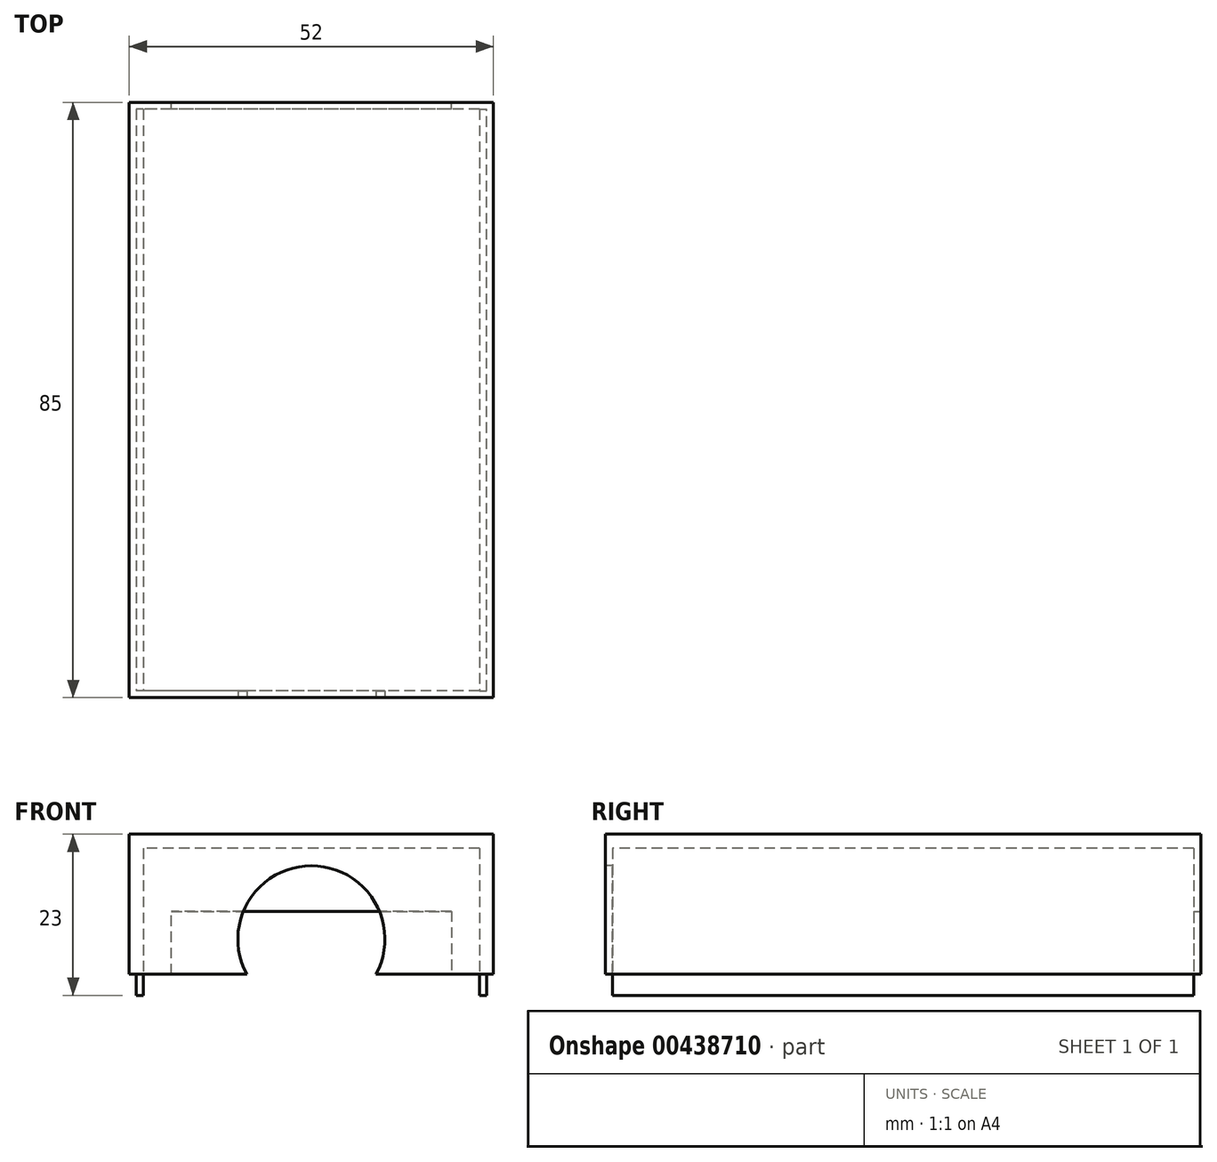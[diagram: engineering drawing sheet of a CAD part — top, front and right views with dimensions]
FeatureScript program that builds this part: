
annotation { "Feature Type Name" : "Feature", "Feature Type Description" : "" }
export const myFeature = defineFeature(function(context is Context, id is Id, definition is map)
    precondition{}
    {
        {
            var Q0;
            Q0=qCreatedBy(makeId("Top.planeOp"),FACE);
            var sketch = newSketch(context, id + "F0", { "sketchPlane" : qUnion([Q0])});
            skLineSegment(sketch, "E0.bottom", {"start": v(26, -42.5) * mm, "end": v(-26, -42.5) * mm});
            skLineSegment(sketch, "E0.top", {"start": v(26, 42.5) * mm, "end": v(-26, 42.5) * mm});
            skLineSegment(sketch, "E0.left", {"start": v(26, -42.5) * mm, "end": v(26, 42.5) * mm});
            skLineSegment(sketch, "E0.right", {"start": v(-26, -42.5) * mm, "end": v(-26, 42.5) * mm});
            skPoint(sketch, "E0.middle", {"position": v(0, 0) * mm});
            skSolve(sketch);
        }
        {
            var Q0;
            Q0 = qSketchRegion(id + "F0", true);
            extrude(context, id + "F1", {"entities" : qUnion([Q0]), "depth" : 20 * mm});
        }
        {
            var Q0;
            Q0=makeQuery(id+"F1.opExtrude","CAP_FACE",FACE,{"disambiguationData":[OSD([sQuery(id+"F0.wireOp",EDGE,"E0.bottom"),sQuery(id+"F0.wireOp",EDGE,"E0.top"),sQuery(id+"F0.wireOp",EDGE,"E0.left"),sQuery(id+"F0.wireOp",EDGE,"E0.right")])],"isStart":true});
            var sketch = newSketch(context, id + "F2", { "sketchPlane" : qUnion([Q0])});
            skLineSegment(sketch, "E1.bottom", {"start": v(24, -41.5) * mm, "end": v(-24, -41.5) * mm});
            skLineSegment(sketch, "E1.top", {"start": v(24, 41.5) * mm, "end": v(-24, 41.5) * mm});
            skLineSegment(sketch, "E1.left", {"start": v(24, -41.5) * mm, "end": v(24, 41.5) * mm});
            skLineSegment(sketch, "E1.right", {"start": v(-24, -41.5) * mm, "end": v(-24, 41.5) * mm});
            skPoint(sketch, "E1.middle", {"position": v(0, 0) * mm});
            skSolve(sketch);
        }
        {
            var Q0;
            Q0=makeQuery(id+"F2.imprint","IMPRINT",FACE,{"disambiguationData":[TD([[makeQuery(id+"F2.imprint","IMPRINT",EDGE,{"derivedFrom":sQuery(id+"F2.wireOp",EDGE,"E1.bottom")}),-1.0]])]});
            extrude(context, id + "F3", {"entities" : qUnion([Q0]), "operationType" : NewBodyOperationType.REMOVE, "oppositeDirection" : true, "depth" : 18 * mm});
        }
        {
            var Q0;
            Q0=makeQuery(id+"F1.opExtrude","CAP_FACE",FACE,{"disambiguationData":[OSD([sQuery(id+"F0.wireOp",EDGE,"E0.bottom"),sQuery(id+"F0.wireOp",EDGE,"E0.top"),sQuery(id+"F0.wireOp",EDGE,"E0.left"),sQuery(id+"F0.wireOp",EDGE,"E0.right")])],"isStart":true});
            var sketch = newSketch(context, id + "F4", { "sketchPlane" : qUnion([Q0])});
            skLineSegment(sketch, "E2.bottom", {"start": v(-24, -41.5) * mm, "end": v(-25, -41.5) * mm});
            skLineSegment(sketch, "E2.top", {"start": v(-24, 41.5) * mm, "end": v(-25, 41.5) * mm});
            skLineSegment(sketch, "E2.left", {"start": v(-24, -41.5) * mm, "end": v(-24, 41.5) * mm});
            skLineSegment(sketch, "E2.right", {"start": v(-25, -41.5) * mm, "end": v(-25, 41.5) * mm});
            skLineSegment(sketch, "E3.bottom", {"start": v(24, 41.5) * mm, "end": v(25, 41.5) * mm});
            skLineSegment(sketch, "E3.top", {"start": v(24, -41.5) * mm, "end": v(25, -41.5) * mm});
            skLineSegment(sketch, "E3.left", {"start": v(24, 41.5) * mm, "end": v(24, -41.5) * mm});
            skLineSegment(sketch, "E3.right", {"start": v(25, 41.5) * mm, "end": v(25, -41.5) * mm});
            skSolve(sketch);
        }
        {
            var Q0;
            Q0=makeQuery(id+"F4.imprint","IMPRINT",FACE,{"disambiguationData":[TD([[makeQuery(id+"F4.imprint","IMPRINT",EDGE,{"derivedFrom":sQuery(id+"F4.wireOp",EDGE,"E2.bottom")}),-1.0]])]});
            var Q1;
            Q1=makeQuery(id+"F4.imprint","IMPRINT",FACE,{"disambiguationData":[TD([[makeQuery(id+"F4.imprint","IMPRINT",EDGE,{"derivedFrom":sQuery(id+"F4.wireOp",EDGE,"E3.bottom")}),-1.0]])]});
            extrude(context, id + "F5", {"entities" : qUnion([Q0, Q1]), "operationType" : NewBodyOperationType.ADD, "depth" : 3 * mm});
        }
        {
            var Q0;
            Q0=makeQuery(id+"F1.opExtrude","SWEPT_FACE",FACE,{"disambiguationData":[OSD([sQuery(id+"F0.wireOp",EDGE,"E0.top")])]});
            var sketch = newSketch(context, id + "F6", { "sketchPlane" : qUnion([Q0])});
            skLineSegment(sketch, "E4", {"start": v(0, 0) * mm, "end": v(20, 0) * mm});
            skLineSegment(sketch, "E5", {"start": v(20, 0) * mm, "end": v(20, 9) * mm});
            skLineSegment(sketch, "E6", {"start": v(20, 9) * mm, "end": v(-20, 9) * mm});
            skLineSegment(sketch, "E7", {"start": v(-20, 9) * mm, "end": v(-20, 0) * mm});
            skLineSegment(sketch, "E8", {"start": v(-20, 0) * mm, "end": v(0, 0) * mm});
            skSolve(sketch);
        }
        {
            var Q0;
            Q0=makeQuery(id+"F6.imprint","IMPRINT",FACE,{"disambiguationData":[TD([[makeQuery(id+"F6.imprint","IMPRINT",EDGE,{"derivedFrom":sQuery(id+"F6.wireOp",EDGE,"E4")}),1.0]])]});
            extrude(context, id + "F7", {"entities" : qUnion([Q0]), "operationType" : NewBodyOperationType.REMOVE, "oppositeDirection" : true, "depth" : 25 * mm});
        }
        {
            var Q0;
            Q0=makeQuery(id+"F1.opExtrude","SWEPT_FACE",FACE,{"disambiguationData":[OSD([sQuery(id+"F0.wireOp",EDGE,"E0.bottom")])]});
            var sketch = newSketch(context, id + "F8", { "sketchPlane" : qUnion([Q0])});
            skLineSegment(sketch, "E9", {"start": v(0, 20) * mm, "end": v(0, 5) * mm});
            skPoint(sketch, "E9.endSnap0", {"position": v(0, 0) * mm});
            skCircle(sketch, "E10", {"center": v(0, 5) * mm, "radius": 10.5 * mm});
            skSolve(sketch);
        }
        {
            var Q0;
            {var subQ0=sQuery(id+"F8.wireOp",EDGE,"E10");var subQ1=makeQuery(id+"F8.imprint","INTERSECT",VERTEX,{"derivedFrom":[sQuery(id+"F8.wireOp",EDGE,"E9"),subQ0]});Q0=makeQuery(id+"F8.imprint","IMPRINT",FACE,{"disambiguationData":[TD([[makeQuery(id+"F8.imprint","IMPRINT",EDGE,{"disambiguationData":[TD([[subQ1,-1.0]])],"derivedFrom":subQ0}),1.0]])]});}
            extrude(context, id + "F9", {"entities" : qUnion([Q0]), "operationType" : NewBodyOperationType.REMOVE, "oppositeDirection" : true, "depth" : 25 * mm});
        }
    });
